# Revit family: NBS_DudleyIndustriesLimited_SntryTwlDpnsrs
name_source: partatom
category: Furniture
units: mm (PartAtom-declared; Revit-internal decimal feet)

## family parameters
Cut with Voids When Loaded = No
Host = Face
Render Appearance Source = Family Geometry
Room Calculation Point = No
Shared = No

## types (1)
- FreeVendCompactSanitaryProductsDispenser
    AssetType = Fixed
    BIMObjectName = NBS_DudleyIndustriesLimited_SanitaryTowelDispensers_FreeVendCompactSanitaryProductsDispenser
    Category = Pr_40_70_22_75:Sanitary towel dispensers
    Default Elevation = 800 mm  [stored 2.62467 ft]
    Description = Free-to-use general sanitary product dispenser featuring adjustable internal columns and vertical stop plates, designed to accommodate a wide range of sanitary products.
    DimensionsDepth = 130 mm
    DimensionsHeight = 287 mm
    DimensionsWidth = 324 mm
    DispenserMaterial = NBS_DudleyIndustriesLimited_StainlessSteel_Brushed
    DurationUnit = year
    Finish = Powder-coated,Brushed
    Form = Wall-mounted
    Height = 287 mm  [stored 0.941601 ft]
    IfcExportAs = IfcFurnitureType
    IfcExportType = USERDEFINED
    IntegralAccessories = Adjustable internal columns.Adjustable vertical stop plate
    ManufacturerName = Dudley Industries Limited
    ManufacturerURL = https://www.dudleyindustries.com
    Material = Stainless steel
    MaterialsBody = Stainless steel
    MaterialsFinishAndColour = Powder-coated, white,Powder-coated, black,Brushed stainless steel
    ModelReference = FreeVend Compact Sanitary Products Dispenser
    NBSInstanceId = 6dd16f3e-2544-480e-acfb-b0e01cce5ca1
    NBSObjectId = 5fc0a8e3-d82a-4a39-b76d-6c4c68a286a0
    NBSVariantId = 00000000-0000-0000-0000-000000000000
    Name = SanitaryTowelDispensers_FreeVendCompactSanitaryProductsDispenser_DudleyIndustriesLimited
    NominalHeight = 0 mm  [stored 0 ft]
    NominalLength = 0 mm  [stored 0 ft]
    NominalWidth = 0 mm  [stored 0 ft]
    Operation = Pull-out
    ProductInformation = https://source.thenbs.com
    Shape = Rectangle
    Uniclass2015Code = Pr_40_70_22_75
    Uniclass2015Title = Sanitary towel dispensers
    Uniclass2015Version = Products v1.36
    Version = 1
    WarrantyDescription = Ten year
    WarrantyDurationUnit = year

note: [stored X ft] marks values corroborated as IEEE doubles in the binary element streams (Revit-internal decimal feet)

## geometry (parser evidence)
native form markers: Sweep x3
no freeform markers — native parametric forms only
